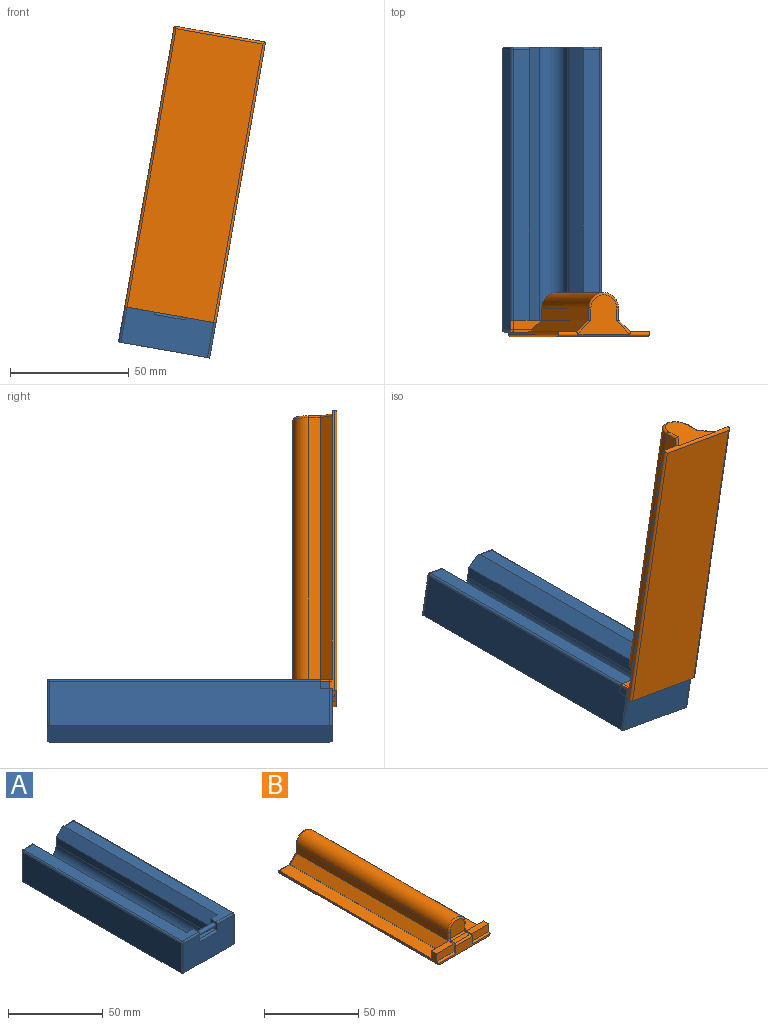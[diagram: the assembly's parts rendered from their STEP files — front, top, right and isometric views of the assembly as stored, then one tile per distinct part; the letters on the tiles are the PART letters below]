
ASSEMBLY  parts=2 mates=1
PART A: 35 faces, bbox 39x120x20 mm
  f0: plane 118x12mm, normal (0,0,1), area 846mm2, adj f9,f13,f17,f29,f31,f32
  f1: plane 13x11.5mm, normal (0,1,0), area 131.4mm2, adj f10,f11,f12,f16
  f2: plane 5x5mm, normal (0,1,0), area 12.5mm2, adj f7,f14,f15
  f3: plane 37x19mm, normal (0,1,0), area 503.6mm2, adj f8,f10,f11,f12,f13,f14,f20,f21
  f4: plane 118x19mm, normal (1,0,0), area 2242mm2, adj f8,f28,f31,f34
  f5: plane 118x19mm, normal (-1,0,0), area 2242mm2, adj f8,f20,f23,f24
  f6: plane 37x19mm, normal (0,-1,0), area 638mm2, adj f8,f15,f17,f23,f26,f27,f28,f29
  f7: plane 118x12mm, normal (0,0,1), area 846mm2, adj f2,f14,f15,f21,f24,f26
  f8: plane 120x39mm, normal (0,0,-1), area 4679.1mm2, adj f3,f4,f5,f6,f20,f23,f28,f34
  f9: plane 5x5mm, normal (0,1,0), area 12.5mm2, adj f0,f13,f17
  f10: plane 115x5mm, normal (-1,0,0), area 575mm2, adj f1,f3,f12,f13
  f11: plane 115x5mm, normal (1,0,0), area 575mm2, adj f1,f3,f12,f14
  f12: cylinder r=6.5mm len=115mm, axis (0,1,0), area 2348.3mm2, adj f1,f3,f10,f11
  f13: plane 115x5mm, normal (-0.71,0,0.71), area 812.9mm2, adj f0,f3,f9,f10,f32
  f14: plane 115x5mm, normal (0.71,0,0.71), area 812.9mm2, adj f2,f3,f7,f11,f21
  f15: plane 6x5mm, normal (1,0,0), area 25mm2, adj f2,f6,f7,f16,f26,f27
  f16: plane 13x4mm, normal (0,0,1), area 52mm2, adj f1,f15,f17,f27
  f17: plane 6x5mm, normal (-1,0,0), area 20.1mm2, adj f0,f6,f9,f16,f18,f27,f29
  f18: cylinder r=1.25mm len=12.97mm, axis (1,0,0), area 101.9mm2, adj f17,f19
  f19: plane 2.5x2.5mm, normal (-1,0,0), area 4.9mm2, adj f18
  f20: cylinder r=1mm len=19mm, axis (0,0,-1), area 29.8mm2, adj f3,f5,f8,f22
  f21: cylinder r=1mm len=8mm, axis (1,0,0), area 11.6mm2, adj f3,f7,f14,f22
  f22: sphere r=1mm, area 1.6mm2, adj f20,f21,f24
  f23: cylinder r=1mm len=19mm, axis (0,0,1), area 29.8mm2, adj f5,f6,f8,f25
  f24: cylinder r=1mm len=118mm, axis (0,1,0), area 185.4mm2, adj f5,f7,f22,f25
  f25: sphere r=1mm, area 1.6mm2, adj f23,f24,f26
  f26: cylinder r=1mm len=12mm, axis (-1,0,0), area 18.8mm2, adj f6,f7,f15,f25
  f27: cylinder r=1mm len=13mm, axis (-1,0,0), area 20.4mm2, adj f6,f15,f16,f17
  f28: cylinder r=1mm len=19mm, axis (0,0,-1), area 29.8mm2, adj f4,f6,f8,f30
  f29: cylinder r=1mm len=12mm, axis (-1,0,0), area 18.8mm2, adj f0,f6,f17,f30
  f30: sphere r=1mm, area 1.6mm2, adj f28,f29,f31
  f31: cylinder r=1mm len=118mm, axis (0,-1,0), area 185.4mm2, adj f0,f4,f30,f33
  f32: cylinder r=1mm len=8mm, axis (1,0,0), area 11.6mm2, adj f0,f3,f13,f33
  f33: sphere r=1mm, area 1.6mm2, adj f31,f32,f34
  f34: cylinder r=1mm len=19mm, axis (0,0,1), area 29.8mm2, adj f3,f4,f8,f33
PART B: 46 faces, bbox 39x120x19 mm
  f0: plane 22.17x16.5mm, normal (0,1,0), area 199.7mm2, adj f25,f38,f39,f40,f41,f42
  f1: plane 120x6mm, normal (1,0,0), area 139.6mm2, adj f2,f25,f26,f27,f29,f35,f37
  f2: plane 13x4mm, normal (0,0,1), area 52mm2, adj f1,f28,f29,f37
  f3: plane 120x6mm, normal (-1,0,0), area 139.6mm2, adj f4,f23,f24,f25,f31,f33,f34
  f4: plane 13x4mm, normal (0,0,1), area 52mm2, adj f3,f30,f31,f34
  f5: plane 5x1mm, normal (-1,0,0), area 4.2mm2, adj f7,f22,f23,f31
  f6: plane 5x1mm, normal (1,0,0), area 4.2mm2, adj f7,f17,f27,f29
  f7: plane 39x6mm, normal (0,-1,0), area 103.6mm2, adj f5,f6,f10,f20,f23,f24,f26,f27
  f8: plane 113.27x5mm, normal (1,0,0), area 565.1mm2, adj f13,f14,f16,f36,f39
  f9: plane 113.27x5mm, normal (-1,0,0), area 565.1mm2, adj f13,f18,f21,f32,f42
  f10: plane 119x37mm, normal (0,0,-1), area 4403mm2, adj f7,f24,f25,f26
  f11: plane 11x3mm, normal (0,0,1), area 33mm2, adj f17,f19,f20,f22
  f12: plane 11x9.5mm, normal (0,-1,0), area 91.5mm2, adj f14,f15,f18,f19
  f13: cylinder r=6.5mm len=113mm, axis (0,1,0), area 2307.5mm2, adj f8,f9,f15,f40
  f14: cylinder r=1mm len=4mm, axis (0,0,-1), area 6.3mm2, adj f8,f12,f15,f16
  f15: torus R=5.5mm, axis (0,1,0), area 30.3mm2, adj f12,f13,f14,f18
  f16: torus R=2mm, axis (1,0,0), area 3.4mm2, adj f8,f14,f17,f19,f28
  f17: cylinder r=1mm len=4mm, axis (0,-1,0), area 5.7mm2, adj f6,f11,f16,f20,f28
  f18: cylinder r=1mm len=4mm, axis (0,0,1), area 6.3mm2, adj f9,f12,f15,f21
  f19: cylinder r=1mm len=11mm, axis (-1,0,0), area 17.3mm2, adj f11,f12,f16,f21
  f20: cylinder r=1mm len=13mm, axis (-1,0,0), area 19.3mm2, adj f7,f11,f17,f22
  f21: torus R=2mm, axis (1,0,0), area 3.4mm2, adj f9,f18,f19,f22,f30
  f22: cylinder r=1mm len=4mm, axis (0,1,0), area 5.7mm2, adj f5,f11,f20,f21,f30
  f23: cylinder r=1mm len=13mm, axis (-1,0,0), area 20.4mm2, adj f3,f5,f7,f31
  f24: cylinder r=1mm len=120mm, axis (0,-1,0), area 187.9mm2, adj f3,f7,f10,f25
  f25: cylinder r=1mm len=39mm, axis (-1,0,0), area 85.7mm2, adj f0,f1,f3,f10,f24,f26,f33,f35
  f26: cylinder r=1mm len=120mm, axis (0,1,0), area 187.9mm2, adj f1,f7,f10,f25
  f27: cylinder r=1mm len=13mm, axis (-1,0,0), area 20.4mm2, adj f1,f6,f7,f29
  f28: plane 4.73x1mm, normal (-1,0,0), area 4.2mm2, adj f2,f16,f17,f29,f36
  f29: plane 13x5mm, normal (0,-1,0), area 65mm2, adj f1,f2,f6,f27,f28
  f30: plane 4.73x1mm, normal (1,0,0), area 4.2mm2, adj f4,f21,f22,f31,f32
  f31: plane 13x5mm, normal (0,-1,0), area 65mm2, adj f3,f4,f5,f23,f30
  f32: plane 114x5mm, normal (-0.71,0,0.71), area 806.1mm2, adj f9,f30,f33,f34,f41
  f33: plane 114x8mm, normal (0,0,1), area 912mm2, adj f3,f25,f32,f34
  f34: plane 13x5mm, normal (0,1,0), area 52.5mm2, adj f3,f4,f32,f33
  f35: plane 114x8mm, normal (0,0,1), area 912mm2, adj f1,f25,f36,f37
  f36: plane 114x5mm, normal (0.71,0,0.71), area 806.1mm2, adj f8,f28,f35,f37,f38
  f37: plane 13x5mm, normal (0,1,0), area 52.5mm2, adj f1,f2,f35,f36
  f38: cylinder r=1mm len=6.29mm, axis (-0.71,0,0.71), area 11.6mm2, adj f0,f25,f36,f39
  f39: cylinder r=1mm len=5.41mm, axis (0,0,1), area 8.1mm2, adj f0,f8,f38,f40
  f40: torus R=5.5mm, axis (0,-1,0), area 30.3mm2, adj f0,f13,f39,f42
  f41: cylinder r=1mm len=6.29mm, axis (-0.71,0,-0.71), area 11.6mm2, adj f0,f25,f32,f42
  f42: cylinder r=1mm len=5.41mm, axis (0,0,-1), area 8.1mm2, adj f0,f9,f40,f41
  f43: plane 2.5x2.5mm, normal (1,0,0), area 4.9mm2, adj f45
  f44: plane 2.5x2.5mm, normal (-1,0,0), area 4.9mm2, adj f45
  f45: cylinder r=1.25mm len=13mm, axis (1,0,0), area 102.1mm2, adj f43,f44
PLACE A rot(axis=(0,1,0),10deg) t=(-26.24,-105.09,50.2)mm
PLACE B rot(axis=(-0.06,-0.71,-0.71),172.9deg) t=(-13.2,-167.09,124.06)mm
MATE cylindrical B.f45 <-> A.f18  axis (-0.98,0,0.17) through (-23.19,-162.59,67.43)mm
